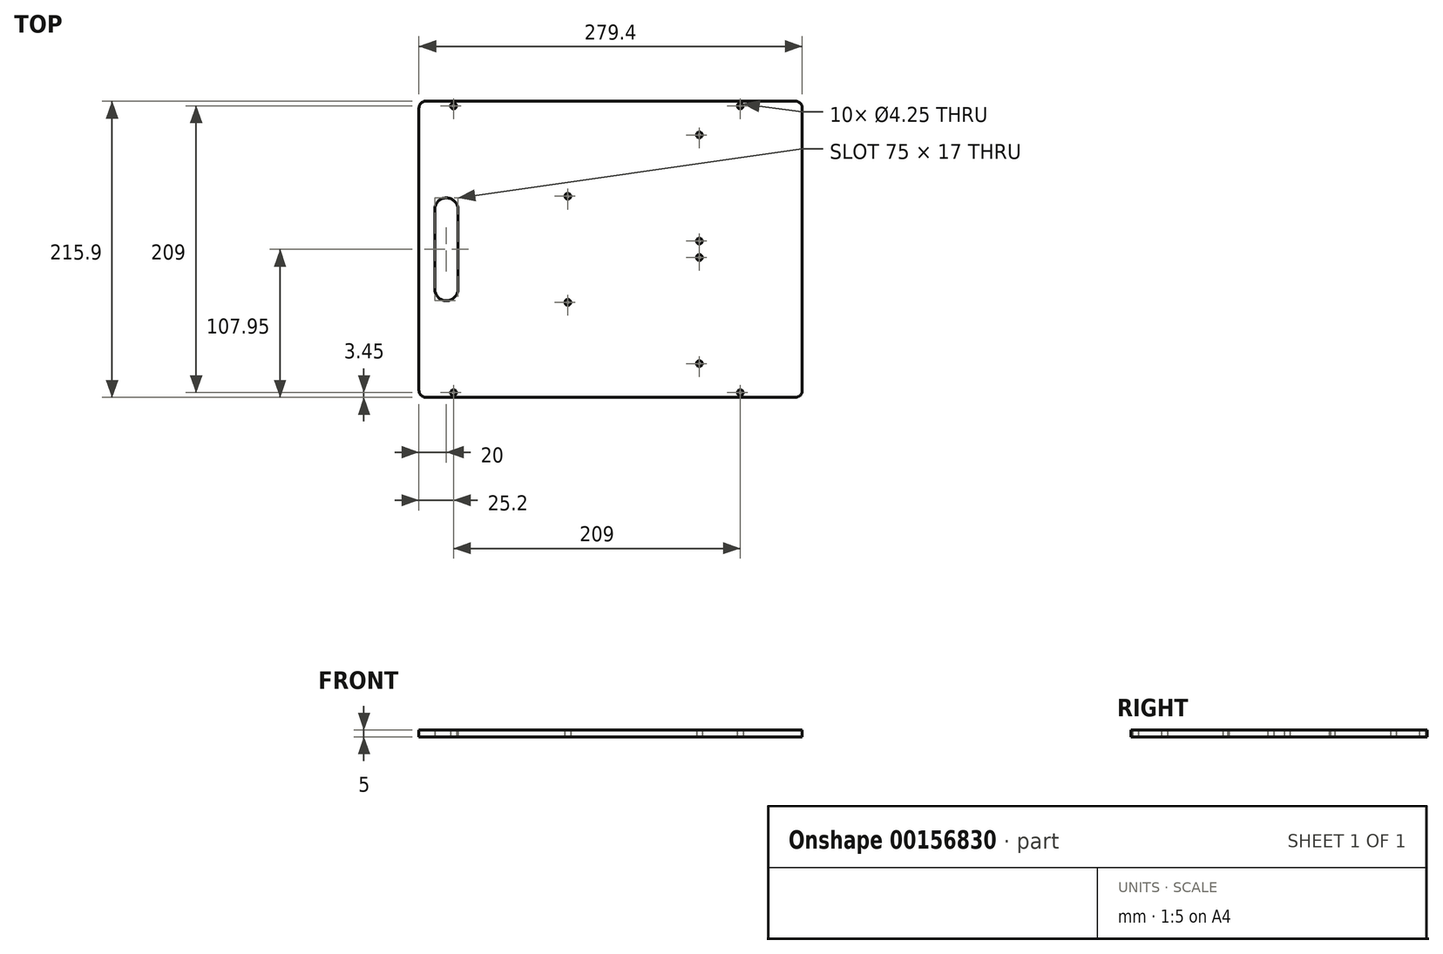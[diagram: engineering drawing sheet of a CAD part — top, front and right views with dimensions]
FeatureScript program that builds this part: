
annotation { "Feature Type Name" : "Feature", "Feature Type Description" : "" }
export const myFeature = defineFeature(function(context is Context, id is Id, definition is map)
    precondition{}
    {
        {
            var Q0;
            Q0=qCreatedBy(makeId("Top.planeOp"),FACE);
            var sketch = newSketch(context, id + "F0", { "sketchPlane" : qUnion([Q0])});
            skLineSegment(sketch, "E0.bottom", {"start": v(134.7, -107.95) * mm, "end": v(-134.7, -107.95) * mm});
            skLineSegment(sketch, "E0.top", {"start": v(134.7, 107.95) * mm, "end": v(-134.7, 107.95) * mm});
            skLineSegment(sketch, "E0.left", {"start": v(139.7, -102.95) * mm, "end": v(139.7, 0) * mm});
            skLineSegment(sketch, "E0.right", {"start": v(-139.7, -102.95) * mm, "end": v(-139.7, 0) * mm});
            skPoint(sketch, "E0.middle", {"position": v(0, 0) * mm});
            skPoint(sketch, "E1.visualSharp", {"position": v(-139.7, 107.95) * mm});
            skArc(sketch, "E1.filletArc", {"start": v(-134.7, 107.95) * mm, "mid": v(-138.24, 106.49) * mm, "end": v(-139.7, 102.95) * mm});
            skPoint(sketch, "E2.visualSharp", {"position": v(-139.7, -107.95) * mm});
            skArc(sketch, "E2.filletArc", {"start": v(-139.7, -102.95) * mm, "mid": v(-138.24, -106.49) * mm, "end": v(-134.7, -107.95) * mm});
            skPoint(sketch, "E3.visualSharp", {"position": v(139.7, -107.95) * mm});
            skArc(sketch, "E3.filletArc", {"start": v(134.7, -107.95) * mm, "mid": v(138.24, -106.49) * mm, "end": v(139.7, -102.95) * mm});
            skPoint(sketch, "E4.visualSharp", {"position": v(139.7, 107.95) * mm});
            skArc(sketch, "E4.filletArc", {"start": v(139.7, 102.95) * mm, "mid": v(138.24, 106.49) * mm, "end": v(134.7, 107.95) * mm});
            skCircle(sketch, "E5", {"center": v(-133.7, 0) * mm, "radius": 2.12 * mm, "construction": true});
            skCircle(sketch, "E6", {"center": v(-133.7, 40) * mm, "radius": 2.12 * mm, "construction": true});
            skCircle(sketch, "E7", {"center": v(-133.7, -40) * mm, "radius": 2.12 * mm, "construction": true});
            skCircle(sketch, "E8.MirrorC", {"center": v(133.7, -40) * mm, "radius": 2.12 * mm, "construction": true});
            skCircle(sketch, "E9.MirrorC", {"center": v(133.7, 40) * mm, "radius": 2.12 * mm, "construction": true});
            skCircle(sketch, "E10.MirrorC", {"center": v(133.7, 0) * mm, "radius": 2.12 * mm, "construction": true});
            skLineSegment(sketch, "E11.trimOffspring", {"start": v(-139.7, 0) * mm, "end": v(-139.7, 102.95) * mm});
            skLineSegment(sketch, "E12.trimOffspring", {"start": v(139.7, 0) * mm, "end": v(139.7, 102.95) * mm});
            skLineSegment(sketch, "E13.bottom", {"start": v(119.7, 37.5) * mm, "end": v(119.7, 37.5) * mm});
            skLineSegment(sketch, "E13.top", {"start": v(119.7, -37.5) * mm, "end": v(119.7, -37.5) * mm});
            skLineSegment(sketch, "E13.left", {"start": v(128.2, 29) * mm, "end": v(128.2, -29) * mm, "construction": true});
            skLineSegment(sketch, "E13.right", {"start": v(111.2, 29) * mm, "end": v(111.2, -29) * mm, "construction": true});
            skPoint(sketch, "E13.middle", {"position": v(119.7, 0) * mm});
            skPoint(sketch, "E14.visualSharp", {"position": v(111.2, 37.5) * mm});
            skArc(sketch, "E14.filletArc", {"start": v(119.7, 37.5) * mm, "mid": v(113.69, 35.01) * mm, "end": v(111.2, 29) * mm, "construction": true});
            skPoint(sketch, "E15.visualSharp", {"position": v(128.2, 37.5) * mm});
            skArc(sketch, "E15.filletArc", {"start": v(128.2, 29) * mm, "mid": v(125.71, 35.01) * mm, "end": v(119.7, 37.5) * mm, "construction": true});
            skPoint(sketch, "E16.visualSharp", {"position": v(128.2, -37.5) * mm});
            skArc(sketch, "E16.filletArc", {"start": v(119.7, -37.5) * mm, "mid": v(125.71, -35.01) * mm, "end": v(128.2, -29) * mm, "construction": true});
            skPoint(sketch, "E17.visualSharp", {"position": v(111.2, -37.5) * mm});
            skArc(sketch, "E17.filletArc", {"start": v(111.2, -29) * mm, "mid": v(113.69, -35.01) * mm, "end": v(119.7, -37.5) * mm, "construction": true});
            skLineSegment(sketch, "E18", {"start": v(114.8, 107.95) * mm, "end": v(114.8, -107.95) * mm, "construction": true});
            skCircle(sketch, "E19", {"center": v(105.8, -40) * mm, "radius": 2.12 * mm, "construction": true});
            skCircle(sketch, "E20", {"center": v(105.8, 40) * mm, "radius": 2.12 * mm, "construction": true});
            skCircle(sketch, "E21", {"center": v(-114.5, 104.5) * mm, "radius": 2.12 * mm});
            skCircle(sketch, "E22", {"center": v(94.5, 104.5) * mm, "radius": 2.12 * mm});
            skCircle(sketch, "E23", {"center": v(-114.5, -104.5) * mm, "radius": 2.12 * mm});
            skCircle(sketch, "E24", {"center": v(94.5, -104.5) * mm, "radius": 2.12 * mm});
            skCircle(sketch, "E25", {"center": v(105.8, 0) * mm, "radius": 2.12 * mm, "construction": true});
            skPoint(sketch, "E25.centerSnap0", {"position": v(111.2, 0) * mm});
            skLineSegment(sketch, "E26.MirrorCS", {"start": v(-111.2, 29) * mm, "end": v(-111.2, -29) * mm});
            skArc(sketch, "E27.MirrorCS", {"start": v(-111.2, -29) * mm, "mid": v(-113.69, -35.01) * mm, "end": v(-119.7, -37.5) * mm});
            skArc(sketch, "E28.MirrorCS", {"start": v(-119.7, -37.5) * mm, "mid": v(-125.71, -35.01) * mm, "end": v(-128.2, -29) * mm});
            skLineSegment(sketch, "E29.MirrorCS", {"start": v(-128.2, 29) * mm, "end": v(-128.2, -29) * mm});
            skArc(sketch, "E30.MirrorCS", {"start": v(-128.2, 29) * mm, "mid": v(-125.71, 35.01) * mm, "end": v(-119.7, 37.5) * mm});
            skArc(sketch, "E31.MirrorCS", {"start": v(-119.7, 37.5) * mm, "mid": v(-113.69, 35.01) * mm, "end": v(-111.2, 29) * mm});
            skCircle(sketch, "E32", {"center": v(125.6, 25) * mm, "radius": 5 * mm, "construction": true});
            skCircle(sketch, "E33", {"center": v(125.6, -25) * mm, "radius": 5 * mm, "construction": true});
            skLineSegment(sketch, "E34.bottom", {"start": v(94.5, -104.5) * mm, "end": v(-114.5, -104.5) * mm, "construction": true});
            skLineSegment(sketch, "E34.top", {"start": v(94.5, 104.5) * mm, "end": v(-114.5, 104.5) * mm, "construction": true});
            skLineSegment(sketch, "E34.left", {"start": v(94.5, -104.5) * mm, "end": v(94.5, 104.5) * mm, "construction": true});
            skLineSegment(sketch, "E34.right", {"start": v(-114.5, -104.5) * mm, "end": v(-114.5, 104.5) * mm, "construction": true});
            skPoint(sketch, "E34.middle", {"position": v(-10, 0) * mm});
            skCircle(sketch, "E35", {"center": v(-6, 97.95) * mm, "radius": 2.12 * mm, "construction": true});
            skCircle(sketch, "E36", {"center": v(-65, 97.95) * mm, "radius": 2.12 * mm, "construction": true});
            skCircle(sketch, "E37", {"center": v(-56, 77.95) * mm, "radius": 2.12 * mm, "construction": true});
            skCircle(sketch, "E38", {"center": v(-6, 77.95) * mm, "radius": 2.12 * mm, "construction": true});
            skCircle(sketch, "E39", {"center": v(-6, 57.95) * mm, "radius": 2.12 * mm, "construction": true});
            skCircle(sketch, "E40", {"center": v(-83.36, 57.95) * mm, "radius": 2.12 * mm, "construction": true});
            skCircle(sketch, "E41.MirrorC", {"center": v(6, 57.95) * mm, "radius": 2.12 * mm, "construction": true});
            skCircle(sketch, "E42.MirrorC", {"center": v(6, 97.95) * mm, "radius": 2.12 * mm, "construction": true});
            skCircle(sketch, "E43.MirrorC", {"center": v(56, 77.95) * mm, "radius": 2.12 * mm, "construction": true});
            skCircle(sketch, "E44.MirrorC", {"center": v(83.36, 57.95) * mm, "radius": 2.12 * mm, "construction": true});
            skCircle(sketch, "E45.MirrorC", {"center": v(65, 97.95) * mm, "radius": 2.12 * mm, "construction": true});
            skCircle(sketch, "E46.MirrorC", {"center": v(6, 77.95) * mm, "radius": 2.12 * mm, "construction": true});
            skCircle(sketch, "E47", {"center": v(-38.68, -57.95) * mm, "radius": 2.12 * mm, "construction": true});
            skCircle(sketch, "E48.MirrorC", {"center": v(38.68, -57.95) * mm, "radius": 2.12 * mm, "construction": true});
            skCircle(sketch, "E49", {"center": v(64.7, -83.36) * mm, "radius": 2.12 * mm});
            skCircle(sketch, "E50", {"center": v(-31.2, -38.68) * mm, "radius": 2.12 * mm});
            skCircle(sketch, "E51", {"center": v(64.7, -6) * mm, "radius": 2.12 * mm});
            skCircle(sketch, "E52.MirrorC", {"center": v(64.7, 6) * mm, "radius": 2.12 * mm});
            skCircle(sketch, "E53.MirrorC", {"center": v(64.7, 83.36) * mm, "radius": 2.12 * mm});
            skCircle(sketch, "E54.MirrorC", {"center": v(-31.2, 38.68) * mm, "radius": 2.12 * mm});
            skSolve(sketch);
        }
        {
            var Q0;
            Q0=qSketchRegion(id+"F0",true);
            extrude(context, id + "F1", {"entities" : qUnion([Q0]), "endBound" : BoundingType.SYMMETRIC, "depth" : 5 * mm});
        }
    });
